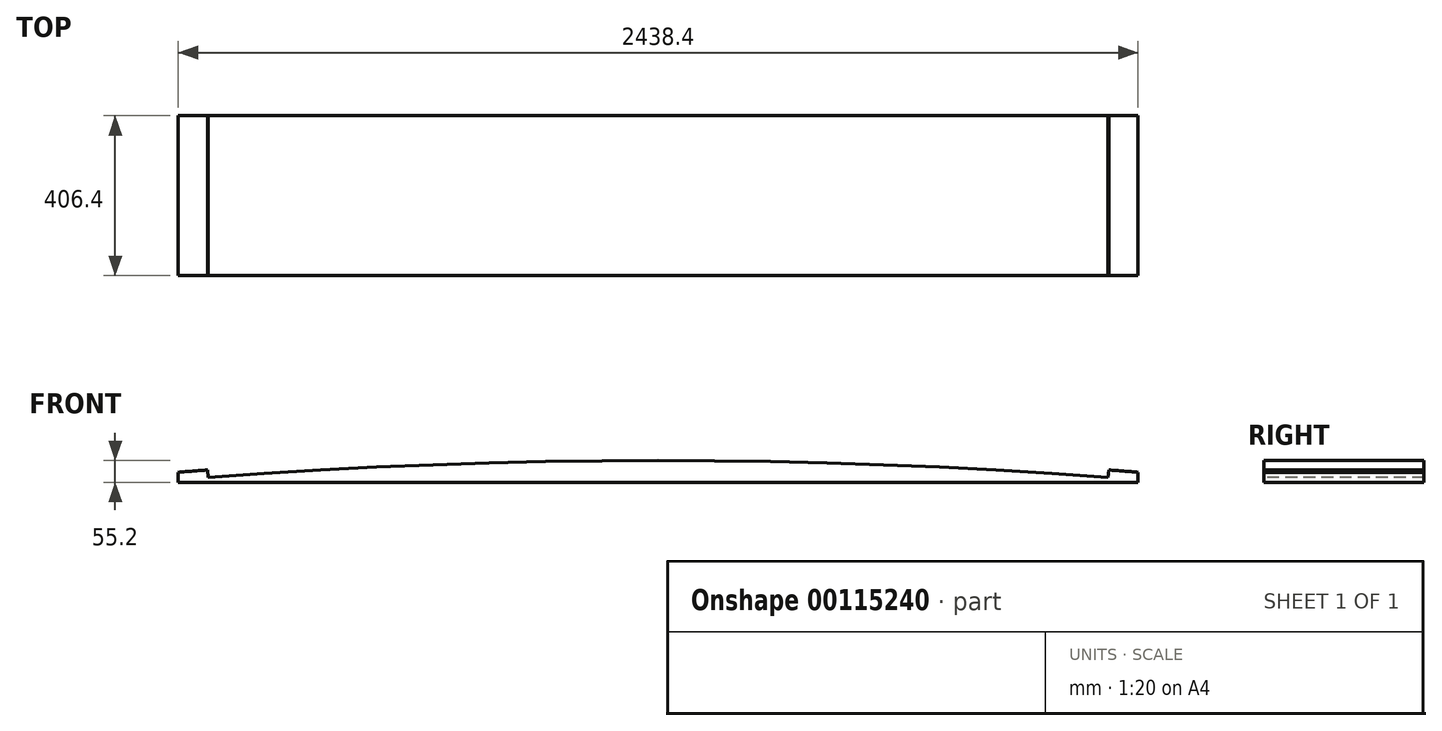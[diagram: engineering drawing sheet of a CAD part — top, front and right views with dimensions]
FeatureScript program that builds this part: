
annotation { "Feature Type Name" : "Feature", "Feature Type Description" : "" }
export const myFeature = defineFeature(function(context is Context, id is Id, definition is map)
    precondition{}
    {
        {
            var Q0;
            Q0=qCreatedBy(makeId("Front.planeOp"),FACE);
            var sketch = newSketch(context, id + "F0", { "sketchPlane" : qUnion([Q0])});
            skArc(sketch, "E0", {"start": v(2362.43, 12.26) * mm, "mid": v(1219.2, 55.2) * mm, "end": v(75.97, 12.26) * mm});
            skPoint(sketch, "E1", {"position": v(1219.2, 55.2) * mm});
            skCircle(sketch, "E2", {"center": v(1219.2, 55.2) * mm, "radius": 546.1 * mm, "construction": true});
            skPoint(sketch, "E3", {"position": v(673.19, 45.41) * mm});
            skArc(sketch, "E4.0", {"start": v(2438.4, 25.46) * mm, "mid": v(2401.13, 28.4) * mm, "end": v(2363.86, 31.25) * mm});
            skLineSegment(sketch, "E5", {"start": v(0, 6.35) * mm, "end": v(0, 25.46) * mm});
            skLineSegment(sketch, "E6", {"start": v(75.97, 12.26) * mm, "end": v(74.54, 31.25) * mm});
            skLineSegment(sketch, "E7", {"start": v(0, 0) * mm, "end": v(0, 6.35) * mm});
            skLineSegment(sketch, "E8", {"start": v(2438.4, 0) * mm, "end": v(0, 0) * mm});
            skLineSegment(sketch, "E9", {"start": v(2438.4, 6.35) * mm, "end": v(2438.4, 0) * mm});
            skLineSegment(sketch, "E10", {"start": v(2438.4, 6.35) * mm, "end": v(2438.4, 25.46) * mm});
            skArc(sketch, "E11.trimOffspring", {"start": v(74.54, 31.25) * mm, "mid": v(37.27, 28.4) * mm, "end": v(0, 25.46) * mm});
            skLineSegment(sketch, "E12", {"start": v(1219.2, 55.2) * mm, "end": v(1219.2, -167.74) * mm, "construction": true});
            skArc(sketch, "E13.MirrorCS", {"start": v(2363.86, 31.25) * mm, "mid": v(2401.13, 28.4) * mm, "end": v(2438.4, 25.46) * mm});
            skLineSegment(sketch, "E14.MirrorCS", {"start": v(2362.43, 12.26) * mm, "end": v(2363.86, 31.25) * mm});
            skLineSegment(sketch, "E15", {"start": v(965.2, 273.22) * mm, "end": v(965.2, -209.87) * mm, "construction": true});
            skPoint(sketch, "E16", {"position": v(965.2, 53.08) * mm});
            skSolve(sketch);
        }
        {
            var Q0;
            Q0=makeQuery(id+"F0.imprint","IMPRINT",FACE,{"disambiguationData":[TD([[makeQuery(id+"F0.imprint","IMPRINT",EDGE,{"derivedFrom":sQuery(id+"F0.wireOp",EDGE,"E0")}),1.0]])]});
            extrude(context, id + "F1", {"entities" : qUnion([Q0]), "oppositeDirection" : true, "depth" : 406.4 * mm});
        }
    });
